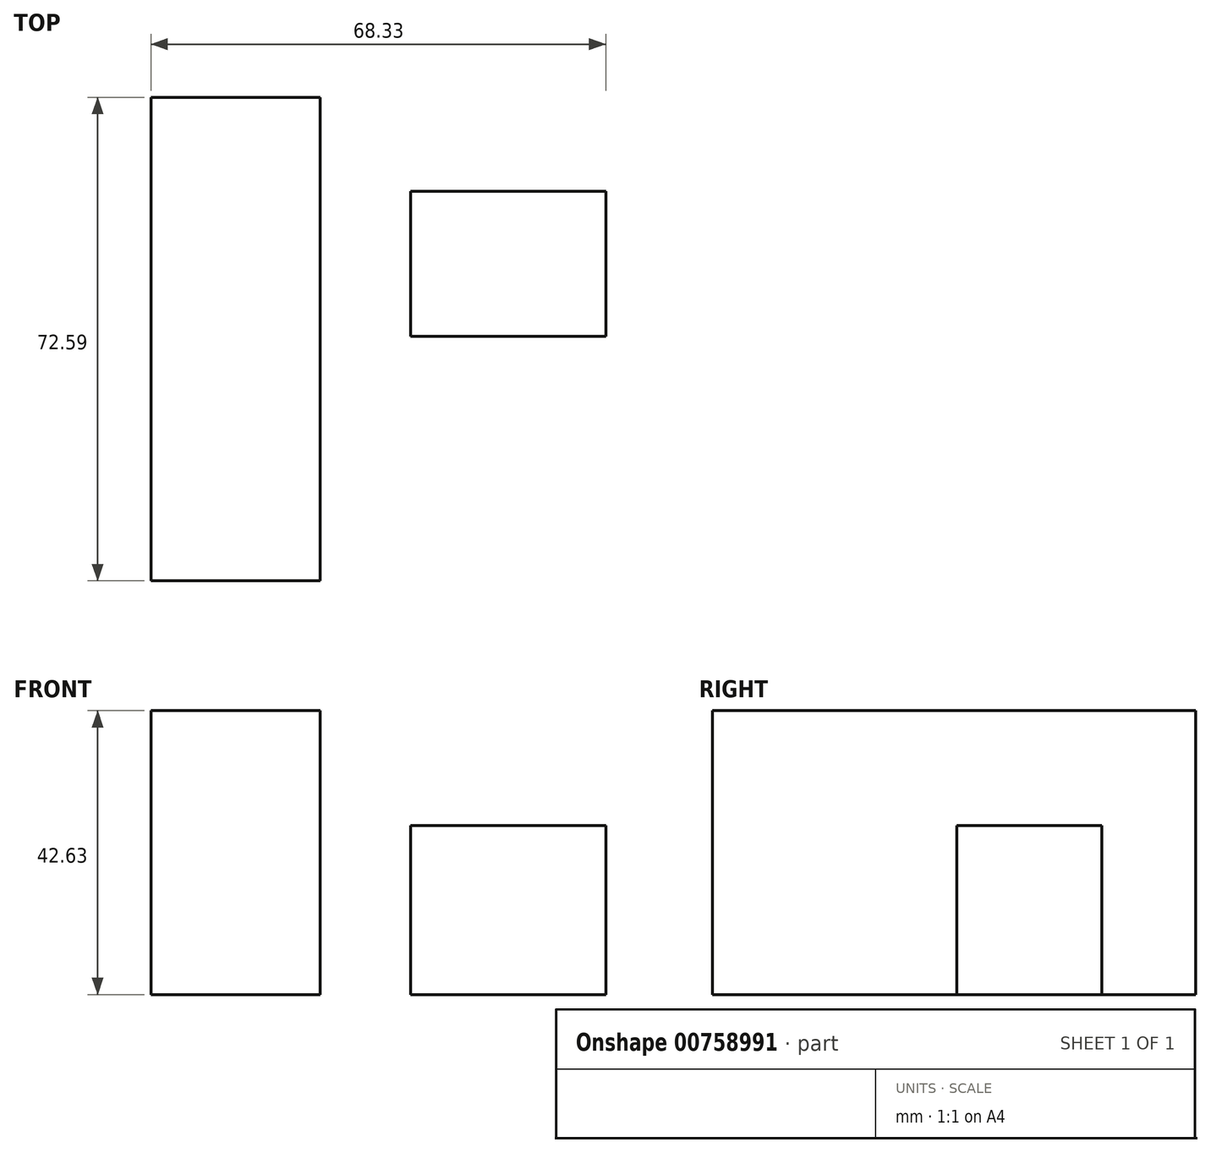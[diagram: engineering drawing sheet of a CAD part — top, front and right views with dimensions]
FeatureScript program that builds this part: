
annotation { "Feature Type Name" : "Feature", "Feature Type Description" : "" }
export const myFeature = defineFeature(function(context is Context, id is Id, definition is map)
    precondition{}
    {
        {
            var Q0;
            Q0=qCreatedBy(makeId("Right.planeOp"),FACE);
            var sketch = newSketch(context, id + "F0", { "sketchPlane" : qUnion([Q0])});
            skLineSegment(sketch, "E0.bottom", {"start": v(-84.18, 42.63) * mm, "end": v(-11.6, 42.63) * mm});
            skLineSegment(sketch, "E0.top", {"start": v(-84.18, 0) * mm, "end": v(-11.6, 0) * mm});
            skLineSegment(sketch, "E0.left", {"start": v(-84.18, 42.63) * mm, "end": v(-84.18, 0) * mm});
            skLineSegment(sketch, "E0.right", {"start": v(-11.6, 42.63) * mm, "end": v(-11.6, 0) * mm});
            skSolve(sketch);
        }
        {
            var Q0;
            Q0=makeQuery(id+"F0.imprint","IMPRINT",FACE,{"disambiguationData":[TD([[makeQuery(id+"F0.imprint","IMPRINT",EDGE,{"derivedFrom":sQuery(id+"F0.wireOp",EDGE,"E0.bottom")}),-1.0]])]});
            extrude(context, id + "F1", {"entities" : qUnion([Q0]), "oppositeDirection" : true, "depth" : 25.4 * mm, "offsetDistance" : 25.4 * mm});
        }
        {
            var Q0;
            Q0=qCreatedBy(makeId("Top.planeOp"),FACE);
            var sketch = newSketch(context, id + "F2", { "sketchPlane" : qUnion([Q0])});
            skLineSegment(sketch, "E1.bottom", {"start": v(13.6, -25.66) * mm, "end": v(42.93, -25.66) * mm});
            skLineSegment(sketch, "E1.top", {"start": v(13.6, -47.44) * mm, "end": v(42.93, -47.44) * mm});
            skLineSegment(sketch, "E1.left", {"start": v(13.6, -25.66) * mm, "end": v(13.6, -47.44) * mm});
            skLineSegment(sketch, "E1.right", {"start": v(42.93, -25.66) * mm, "end": v(42.93, -47.44) * mm});
            skSolve(sketch);
        }
        {
            var Q0;
            Q0=makeQuery(id+"F2.imprint","IMPRINT",FACE,{"disambiguationData":[TD([[makeQuery(id+"F2.imprint","IMPRINT",EDGE,{"derivedFrom":sQuery(id+"F2.wireOp",EDGE,"E1.bottom")}),-1.0]])]});
            extrude(context, id + "F3", {"entities" : qUnion([Q0]), "depth" : 25.4 * mm, "offsetDistance" : 25.4 * mm});
        }
    });
